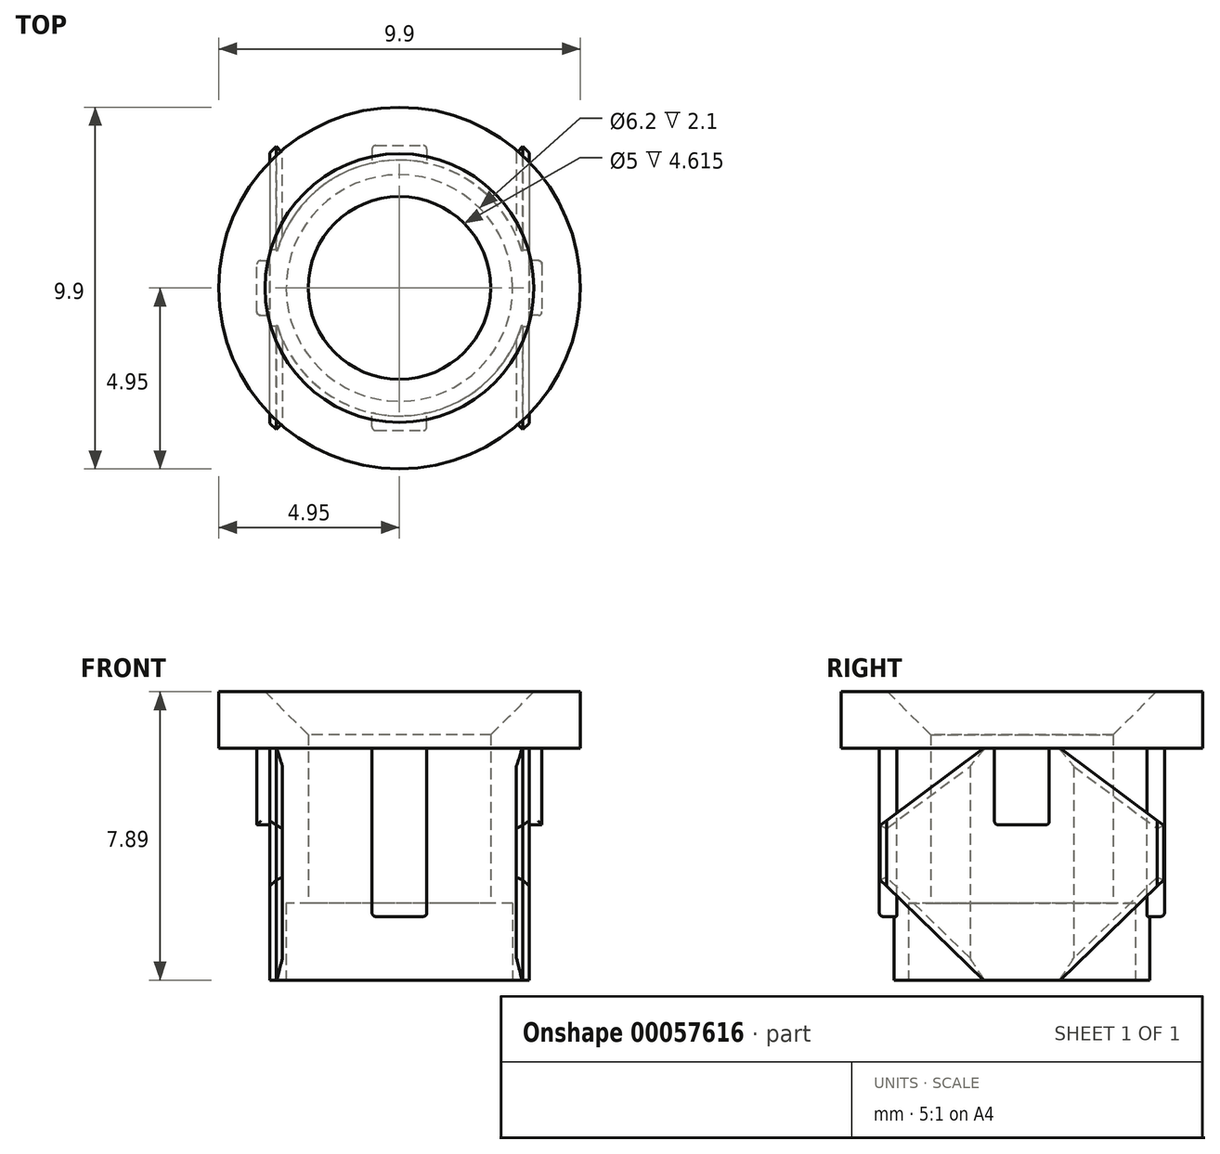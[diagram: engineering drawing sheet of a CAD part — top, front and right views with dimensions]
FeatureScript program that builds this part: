
annotation { "Feature Type Name" : "Feature", "Feature Type Description" : "" }
export const myFeature = defineFeature(function(context is Context, id is Id, definition is map)
    precondition{}
    {
        {
            var Q0;
            Q0=qCreatedBy(makeId("Top.planeOp"),FACE);
            var sketch = newSketch(context, id + "F0", { "sketchPlane" : qUnion([Q0])});
            skCircle(sketch, "E0", {"center": v(0, 0) * mm, "radius": 3.1 * mm});
            skCircle(sketch, "E1", {"center": v(0, 0) * mm, "radius": 3.5 * mm});
            skSolve(sketch);
        }
        {
            var Q0;
            Q0=makeQuery(id+"F0.imprint","IMPRINT",FACE,{"disambiguationData":[TD([[makeQuery(id+"F0.imprint","IMPRINT",EDGE,{"derivedFrom":sQuery(id+"F0.wireOp",EDGE,"E0")}),-1.0]])]});
            extrude(context, id + "F1", {"entities" : qUnion([Q0]), "depth" : 2.1 * mm});
        }
        {
            var Q0;
            Q0=makeQuery(id+"F1.opExtrude","CAP_FACE",FACE,{"disambiguationData":[OSD([sQuery(id+"F0.wireOp",EDGE,"E0"),sQuery(id+"F0.wireOp",EDGE,"E1")])],"isStart":false});
            var sketch = newSketch(context, id + "F2", { "sketchPlane" : qUnion([Q0])});
            skCircle(sketch, "E2", {"center": v(0, 0) * mm, "radius": 2.5 * mm});
            skSolve(sketch);
        }
        {
            var Q0;
            Q0=makeQuery(id+"F2.imprint","IMPRINT",FACE,{"disambiguationData":[TD([[makeQuery(id+"F2.imprint","IMPRINT",EDGE,{"derivedFrom":sQuery(id+"F2.wireOp",EDGE,"E2")}),-1.0]])]});
            var Q1;
            Q1=makeQuery(id+"F2.imprint","IMPRINT",FACE,{"disambiguationData":[TD([[makeQuery(id+"F2.imprint","IMPRINT",EDGE,{"derivedFrom":makeQuery(id+"F1.opExtrude","CAP_EDGE",EDGE,{"disambiguationData":[OSD([sQuery(id+"F0.wireOp",EDGE,"E0")])],"isStart":false})}),-1.0]])]});
            extrude(context, id + "F3", {"entities" : qUnion([Q0, Q1]), "operationType" : NewBodyOperationType.ADD, "depth" : 4.24 * mm});
        }
        {
            var Q0;
            Q0=makeQuery(id+"F3.opExtrude","CAP_FACE",FACE,{"disambiguationData":[OSD([sQuery(id+"F0.wireOp",EDGE,"E1"),sQuery(id+"F2.wireOp",EDGE,"E2")])],"isStart":false});
            var sketch = newSketch(context, id + "F4", { "sketchPlane" : qUnion([Q0])});
            skCircle(sketch, "E3", {"center": v(0, 0) * mm, "radius": 4.95 * mm});
            skCircle(sketch, "E4", {"center": v(0, 0) * mm, "radius": 2.5 * mm});
            skSolve(sketch);
        }
        {
            var Q0;
            Q0=makeQuery(id+"F4.imprint","IMPRINT",FACE,{"disambiguationData":[TD([[makeQuery(id+"F4.imprint","IMPRINT",EDGE,{"derivedFrom":sQuery(id+"F4.wireOp",EDGE,"E3")}),1.0]])]});
            var Q1;
            Q1=makeQuery(id+"F4.imprint","IMPRINT",FACE,{"disambiguationData":[TD([[makeQuery(id+"F4.imprint","IMPRINT",EDGE,{"derivedFrom":sQuery(id+"F4.wireOp",EDGE,"E4")}),-1.0]])]});
            extrude(context, id + "F5", {"entities" : qUnion([Q0, Q1]), "operationType" : NewBodyOperationType.ADD, "depth" : 1.55 * mm});
        }
        {
            var Q0;
            Q0=makeQuery(id+"F5.opExtrude","CAP_EDGE",EDGE,{"disambiguationData":[OSD([sQuery(id+"F4.wireOp",EDGE,"E4")])],"isStart":false});
            chamfer(context, id + "F6", {"entities" : qUnion([Q0]), "width" : 1.18 * mm, "tangentPropagation" : true});
        }
        {
            var Q0;
            Q0=makeQuery(id+"F5.opExtrude","CAP_FACE",FACE,{"disambiguationData":[OSD([sQuery(id+"F4.wireOp",EDGE,"E3"),sQuery(id+"F4.wireOp",EDGE,"E4")])],"isStart":true});
            var sketch = newSketch(context, id + "F7", { "sketchPlane" : qUnion([Q0])});
            skLineSegment(sketch, "E5", {"start": v(0, 3.5) * mm, "end": v(0, 3.68) * mm, "construction": true});
            skLineSegment(sketch, "E6", {"start": v(0, 3.5) * mm, "end": v(0, 3.7) * mm, "construction": true});
            skLineSegment(sketch, "E7", {"start": v(0, -3.5) * mm, "end": v(0, -3.9) * mm, "construction": true});
            skLineSegment(sketch, "E8", {"start": v(0, -3.9) * mm, "end": v(0.75, -3.9) * mm});
            skLineSegment(sketch, "E9", {"start": v(0, -3.9) * mm, "end": v(-0.75, -3.9) * mm});
            skLineSegment(sketch, "E10", {"start": v(0.75, -3.9) * mm, "end": v(0.75, -3.42) * mm});
            skLineSegment(sketch, "E11", {"start": v(-0.75, -3.9) * mm, "end": v(-0.75, -3.42) * mm});
            skLineSegment(sketch, "E12.MirrorCS", {"start": v(0, 3.5) * mm, "end": v(0, 3.9) * mm, "construction": true});
            skLineSegment(sketch, "E13.MirrorCS", {"start": v(0, 3.9) * mm, "end": v(-0.75, 3.9) * mm});
            skLineSegment(sketch, "E14.MirrorCS", {"start": v(0, 3.9) * mm, "end": v(0.75, 3.9) * mm});
            skLineSegment(sketch, "E15.MirrorCS", {"start": v(0.75, 3.9) * mm, "end": v(0.75, 3.42) * mm});
            skLineSegment(sketch, "E16.MirrorCS", {"start": v(-0.75, 3.9) * mm, "end": v(-0.75, 3.42) * mm});
            skLineSegment(sketch, "E17", {"start": v(0, 0) * mm, "end": v(-2.98, -2.98) * mm, "construction": true});
            skLineSegment(sketch, "E18.MirrorCS", {"start": v(0, 0) * mm, "end": v(2.98, -2.98) * mm, "construction": true});
            skLineSegment(sketch, "E19.MirrorCS", {"start": v(3.9, 0.75) * mm, "end": v(3.42, 0.75) * mm});
            skLineSegment(sketch, "E20.MirrorCS", {"start": v(3.9, 0) * mm, "end": v(3.9, 0.75) * mm});
            skLineSegment(sketch, "E21.MirrorCS", {"start": v(3.9, 0) * mm, "end": v(3.9, -0.75) * mm});
            skLineSegment(sketch, "E22.MirrorCS", {"start": v(3.9, -0.75) * mm, "end": v(3.42, -0.75) * mm});
            skLineSegment(sketch, "E23.MirrorCS", {"start": v(3.5, 0) * mm, "end": v(3.9, 0) * mm, "construction": true});
            skLineSegment(sketch, "E24.MirrorCS", {"start": v(-3.9, -0.75) * mm, "end": v(-3.42, -0.75) * mm});
            skLineSegment(sketch, "E25.MirrorCS", {"start": v(-3.5, 0) * mm, "end": v(-3.9, 0) * mm, "construction": true});
            skLineSegment(sketch, "E26.MirrorCS", {"start": v(-3.9, 0.75) * mm, "end": v(-3.42, 0.75) * mm});
            skLineSegment(sketch, "E27.MirrorCS", {"start": v(-3.9, 0) * mm, "end": v(-3.9, 0.75) * mm});
            skLineSegment(sketch, "E28.MirrorCS", {"start": v(-3.9, 0) * mm, "end": v(-3.9, -0.75) * mm});
            skSolve(sketch);
        }
        {
            var Q0;
            Q0=makeQuery(id+"F7.imprint","IMPRINT",FACE,{"disambiguationData":[TD([[makeQuery(id+"F7.imprint","IMPRINT",EDGE,{"derivedFrom":sQuery(id+"F7.wireOp",EDGE,"E8")}),1.0]])]});
            var Q1;
            Q1=makeQuery(id+"F7.imprint","IMPRINT",FACE,{"disambiguationData":[TD([[makeQuery(id+"F7.imprint","IMPRINT",EDGE,{"derivedFrom":sQuery(id+"F7.wireOp",EDGE,"E13.MirrorCS")}),1.0]])]});
            extrude(context, id + "F8", {"entities" : qUnion([Q0, Q1]), "operationType" : NewBodyOperationType.ADD, "depth" : 4.6 * mm});
        }
        {
            var Q0;
            {var subQ1=sQuery(id+"F7.wireOp",EDGE,"E24.MirrorCS");Q0=makeQuery(id+"F7.imprint","IMPRINT",FACE,{"disambiguationData":[TD([[makeQuery(id+"F7.imprint","IMPRINT",EDGE,{"derivedFrom":subQ1}),1.0]])]});}
            var Q1;
            {var subQ1=sQuery(id+"F7.wireOp",EDGE,"E19.MirrorCS");Q1=makeQuery(id+"F7.imprint","IMPRINT",FACE,{"disambiguationData":[TD([[makeQuery(id+"F7.imprint","IMPRINT",EDGE,{"derivedFrom":subQ1}),1.0]])]});}
            extrude(context, id + "F9", {"entities" : qUnion([Q0, Q1]), "operationType" : NewBodyOperationType.ADD, "depth" : 2.09 * mm});
        }
        {
            var Q0;
            Q0=makeQuery(id+"F8.opExtrude","CAP_EDGE",EDGE,{"disambiguationData":[OSD([sQuery(id+"F7.wireOp",EDGE,"E10")])],"isStart":false});
            var Q1;
            Q1=makeQuery(id+"F8.opExtrude","CAP_EDGE",EDGE,{"disambiguationData":[OSD([sQuery(id+"F7.wireOp",EDGE,"E8"),sQuery(id+"F7.wireOp",EDGE,"E9")])],"isStart":false});
            var Q2;
            Q2=makeQuery(id+"F8.opExtrude","SWEPT_EDGE",EDGE,{"disambiguationData":[OSD([sQuery(id+"F7.wireOp",EDGE,"E8"),sQuery(id+"F7.wireOp",EDGE,"E10")])]});
            var Q3;
            Q3=makeQuery(id+"F9.opExtrude","CAP_EDGE",EDGE,{"disambiguationData":[OSD([sQuery(id+"F7.wireOp",EDGE,"E22.MirrorCS")])],"isStart":false});
            var Q4;
            Q4=makeQuery(id+"F9.opExtrude","SWEPT_EDGE",EDGE,{"disambiguationData":[OSD([sQuery(id+"F7.wireOp",EDGE,"E21.MirrorCS"),sQuery(id+"F7.wireOp",EDGE,"E22.MirrorCS")])]});
            var Q5;
            Q5=makeQuery(id+"F9.opExtrude","CAP_EDGE",EDGE,{"disambiguationData":[OSD([sQuery(id+"F7.wireOp",EDGE,"E19.MirrorCS")])],"isStart":false});
            var Q6;
            Q6=makeQuery(id+"F9.opExtrude","SWEPT_EDGE",EDGE,{"disambiguationData":[OSD([sQuery(id+"F7.wireOp",EDGE,"E19.MirrorCS"),sQuery(id+"F7.wireOp",EDGE,"E20.MirrorCS")])]});
            var Q7;
            Q7=makeQuery(id+"F8.opExtrude","CAP_EDGE",EDGE,{"disambiguationData":[OSD([sQuery(id+"F7.wireOp",EDGE,"E13.MirrorCS"),sQuery(id+"F7.wireOp",EDGE,"E14.MirrorCS")])],"isStart":false});
            var Q8;
            Q8=makeQuery(id+"F8.opExtrude","SWEPT_EDGE",EDGE,{"disambiguationData":[OSD([sQuery(id+"F7.wireOp",EDGE,"E14.MirrorCS"),sQuery(id+"F7.wireOp",EDGE,"E15.MirrorCS")])]});
            var Q9;
            Q9=makeQuery(id+"F8.opExtrude","CAP_EDGE",EDGE,{"disambiguationData":[OSD([sQuery(id+"F7.wireOp",EDGE,"E15.MirrorCS")])],"isStart":false});
            var Q10;
            Q10=makeQuery(id+"F8.opExtrude","SWEPT_EDGE",EDGE,{"disambiguationData":[OSD([sQuery(id+"F7.wireOp",EDGE,"E13.MirrorCS"),sQuery(id+"F7.wireOp",EDGE,"E16.MirrorCS")])]});
            var Q11;
            Q11=makeQuery(id+"F8.opExtrude","CAP_EDGE",EDGE,{"disambiguationData":[OSD([sQuery(id+"F7.wireOp",EDGE,"E16.MirrorCS")])],"isStart":false});
            var Q12;
            Q12=makeQuery(id+"F9.opExtrude","SWEPT_EDGE",EDGE,{"disambiguationData":[OSD([sQuery(id+"F7.wireOp",EDGE,"E26.MirrorCS"),sQuery(id+"F7.wireOp",EDGE,"E27.MirrorCS")])]});
            var Q13;
            Q13=makeQuery(id+"F9.opExtrude","CAP_EDGE",EDGE,{"disambiguationData":[OSD([sQuery(id+"F7.wireOp",EDGE,"E27.MirrorCS"),sQuery(id+"F7.wireOp",EDGE,"E28.MirrorCS")])],"isStart":false});
            var Q14;
            Q14=makeQuery(id+"F9.opExtrude","SWEPT_EDGE",EDGE,{"disambiguationData":[OSD([sQuery(id+"F7.wireOp",EDGE,"E24.MirrorCS"),sQuery(id+"F7.wireOp",EDGE,"E28.MirrorCS")])]});
            var Q15;
            Q15=makeQuery(id+"F9.opExtrude","CAP_EDGE",EDGE,{"disambiguationData":[OSD([sQuery(id+"F7.wireOp",EDGE,"E24.MirrorCS")])],"isStart":false});
            var Q16;
            Q16=makeQuery(id+"F9.opExtrude","CAP_EDGE",EDGE,{"disambiguationData":[OSD([sQuery(id+"F7.wireOp",EDGE,"E26.MirrorCS")])],"isStart":false});
            var Q17;
            Q17=makeQuery(id+"F8.opExtrude","SWEPT_EDGE",EDGE,{"disambiguationData":[OSD([sQuery(id+"F7.wireOp",EDGE,"E9"),sQuery(id+"F7.wireOp",EDGE,"E11")])]});
            var Q18;
            Q18=makeQuery(id+"F8.opExtrude","CAP_EDGE",EDGE,{"disambiguationData":[OSD([sQuery(id+"F7.wireOp",EDGE,"E11")])],"isStart":false});
            fillet(context, id + "F10", {"entities" : qUnion([Q0, Q1, Q2, Q3, Q4, Q5, Q6, Q7, Q8, Q9, Q10, Q11, Q12, Q13, Q14, Q15, Q16, Q17, Q18]), "radius" : .1 * mm, "tangentPropagation" : true, "allowEdgeOverflow" : false});
        }
        {
            var Q0;
            Q0=makeQuery(id+"F7.imprint","IMPRINT",FACE,{"disambiguationData":[TD([[makeQuery(id+"F7.imprint","IMPRINT",EDGE,{"derivedFrom":sQuery(id+"F7.wireOp",EDGE,"E8")}),-1.0]])]});
            var sketch = newSketch(context, id + "F11", { "sketchPlane" : qUnion([Q0])});
            skLineSegment(sketch, "E29.bottom", {"start": v(3.2, 0) * mm, "end": v(3.55, 0) * mm});
            skLineSegment(sketch, "E29.top", {"start": v(3.2, -3.88) * mm, "end": v(3.55, -3.88) * mm});
            skLineSegment(sketch, "E29.left", {"start": v(3.2, 0) * mm, "end": v(3.2, -3.88) * mm});
            skLineSegment(sketch, "E29.right", {"start": v(3.55, 0) * mm, "end": v(3.55, -3.88) * mm});
            skLineSegment(sketch, "E30.top", {"start": v(3.2, 3.88) * mm, "end": v(3.55, 3.88) * mm});
            skLineSegment(sketch, "E30.left", {"start": v(3.2, 0) * mm, "end": v(3.2, 3.88) * mm});
            skLineSegment(sketch, "E30.right", {"start": v(3.55, 0) * mm, "end": v(3.55, 3.88) * mm});
            skSolve(sketch);
        }
        {
            var Q0;
            Q0 = qSketchRegion(id + "F11", true);
            extrude(context, id + "F12", {"entities" : qUnion([Q0]), "operationType" : NewBodyOperationType.ADD, "depth" : 6.34 * mm});
        }
        {
            var Q0;
            Q0=makeQuery(id+"F12.opExtrude","SWEPT_FACE",FACE,{"disambiguationData":[OSD([sQuery(id+"F11.wireOp",EDGE,"E29.right"),sQuery(id+"F11.wireOp",EDGE,"E30.right")])]});
            var sketch = newSketch(context, id + "F13", { "sketchPlane" : qUnion([Q0])});
            skLineSegment(sketch, "E31", {"start": v(-3.88, 4.24) * mm, "end": v(-1.05, 6.34) * mm});
            skLineSegment(sketch, "E32.MirrorCS", {"start": v(3.88, 4.24) * mm, "end": v(1.05, 6.34) * mm});
            skLineSegment(sketch, "E33", {"start": v(-3.88, 4.24) * mm, "end": v(-3.87, 2.74) * mm});
            skLineSegment(sketch, "E34", {"start": v(-3.87, 2.74) * mm, "end": v(-1.05, 0) * mm});
            skLineSegment(sketch, "E35.MirrorCS", {"start": v(3.88, 4.24) * mm, "end": v(3.87, 2.74) * mm});
            skLineSegment(sketch, "E36.MirrorCS", {"start": v(3.87, 2.74) * mm, "end": v(1.05, 0) * mm});
            skSolve(sketch);
        }
        {
            var Q0;
            {var subQ0=sQuery(id+"F13.wireOp",EDGE,"E31");Q0=makeQuery(id+"F13.imprint","IMPRINT",FACE,{"disambiguationData":[TD([[makeQuery(id+"F13.imprint","IMPRINT",EDGE,{"derivedFrom":subQ0}),1.0]])]});}
            var Q1;
            {var subQ0=sQuery(id+"F13.wireOp",EDGE,"E32.MirrorCS");Q1=makeQuery(id+"F13.imprint","IMPRINT",FACE,{"disambiguationData":[TD([[makeQuery(id+"F13.imprint","IMPRINT",EDGE,{"derivedFrom":subQ0}),-1.0]])]});}
            var Q2;
            {var subQ0=sQuery(id+"F13.wireOp",EDGE,"E36.MirrorCS");Q2=makeQuery(id+"F13.imprint","IMPRINT",FACE,{"disambiguationData":[TD([[makeQuery(id+"F13.imprint","IMPRINT",EDGE,{"derivedFrom":subQ0}),1.0]])]});}
            var Q3;
            {var subQ0=sQuery(id+"F13.wireOp",EDGE,"E34");Q3=makeQuery(id+"F13.imprint","IMPRINT",FACE,{"disambiguationData":[TD([[makeQuery(id+"F13.imprint","IMPRINT",EDGE,{"derivedFrom":subQ0}),-1.0]])]});}
            extrude(context, id + "F14", {"entities" : qUnion([Q0, Q1, Q2, Q3]), "operationType" : NewBodyOperationType.REMOVE, "oppositeDirection" : true, "depth" : 0.38 * mm});
        }
        {
            var Q0;
            Q0=makeQuery(id+"F1.opExtrude","SWEPT_BODY",BODY,{"disambiguationData":[OSD([sQuery(id+"F0.wireOp",EDGE,"E0"),sQuery(id+"F0.wireOp",EDGE,"E1")])]});
            var Q1;
            Q1=qCreatedBy(makeId("Right.planeOp"),FACE);
            mirror(context, id + "F15", {"operationType" : NewBodyOperationType.ADD, "entities" : qUnion([Q0]), "mirrorPlane" : qUnion([Q1])});
        }
        {
            var Q0;
            Q0=makeQuery(id+"F15.opPattern","COPY",EDGE,{"derivedFrom":makeQuery(id+"F14.boolean.opBoolean","COPY",EDGE,{"derivedFrom":makeQuery(id+"F14.opExtrude","CAP_EDGE",EDGE,{"disambiguationData":[OSD([sQuery(id+"F13.wireOp",EDGE,"E36.MirrorCS")])],"isStart":true})}),"instanceName":"1"});
            var Q1;
            Q1=makeQuery(id+"F15.opPattern","COPY",EDGE,{"derivedFrom":makeQuery(id+"F12.opExtrude","SWEPT_EDGE",EDGE,{"disambiguationData":[OSD([sQuery(id+"F11.wireOp",EDGE,"E29.top"),sQuery(id+"F11.wireOp",EDGE,"E29.right")])]}),"instanceName":"1"});
            var Q2;
            Q2=makeQuery(id+"F15.opPattern","COPY",EDGE,{"derivedFrom":makeQuery(id+"F14.boolean.opBoolean","COPY",EDGE,{"derivedFrom":makeQuery(id+"F14.opExtrude","CAP_EDGE",EDGE,{"disambiguationData":[OSD([sQuery(id+"F13.wireOp",EDGE,"E32.MirrorCS")])],"isStart":true})}),"instanceName":"1"});
            var Q3;
            {var subQ3=sQuery(id+"F11.wireOp",EDGE,"E30.left");var subQ6=sQuery(id+"F11.wireOp",EDGE,"E29.left");var subQ7=sQuery(id+"F11.wireOp",EDGE,"E29.top");Q3=makeQuery(id+"F15.opPattern","COPY",EDGE,{"derivedFrom":makeQuery(id+"F14.boolean.opBoolean","INTERSECT",EDGE,{"derivedFrom":[makeQuery(id+"F12.boolean.opBoolean","SPLIT",FACE,{"disambiguationData":[TD([makeQuery(id+"F12.opExtrude","SWEPT_FACE",FACE,{"disambiguationData":[OSD([subQ7])]})])],"derivedFrom":makeQuery(id+"F12.opExtrude","SWEPT_FACE",FACE,{"disambiguationData":[OSD([subQ6,subQ3])]})}),makeQuery(id+"F14.opExtrude","SWEPT_FACE",FACE,{"disambiguationData":[OSD([sQuery(id+"F13.wireOp",EDGE,"E36.MirrorCS")])]})]}),"instanceName":"1"});}
            var Q4;
            {var subQ3=sQuery(id+"F11.wireOp",EDGE,"E30.left");var subQ6=sQuery(id+"F11.wireOp",EDGE,"E29.left");var subQ7=sQuery(id+"F11.wireOp",EDGE,"E29.top");Q4=makeQuery(id+"F15.opPattern","COPY",EDGE,{"derivedFrom":makeQuery(id+"F14.boolean.opBoolean","INTERSECT",EDGE,{"derivedFrom":[makeQuery(id+"F12.boolean.opBoolean","SPLIT",FACE,{"disambiguationData":[TD([makeQuery(id+"F12.opExtrude","SWEPT_FACE",FACE,{"disambiguationData":[OSD([subQ7])]})])],"derivedFrom":makeQuery(id+"F12.opExtrude","SWEPT_FACE",FACE,{"disambiguationData":[OSD([subQ6,subQ3])]})}),makeQuery(id+"F14.opExtrude","SWEPT_FACE",FACE,{"disambiguationData":[OSD([sQuery(id+"F13.wireOp",EDGE,"E32.MirrorCS")])]})]}),"instanceName":"1"});}
            var Q5;
            Q5=makeQuery(id+"F15.opPattern","COPY",EDGE,{"derivedFrom":makeQuery(id+"F12.opExtrude","SWEPT_EDGE",EDGE,{"disambiguationData":[OSD([sQuery(id+"F11.wireOp",EDGE,"E29.top"),sQuery(id+"F11.wireOp",EDGE,"E29.left")])]}),"instanceName":"1"});
            var Q6;
            Q6=makeQuery(id+"F15.opPattern","COPY",EDGE,{"derivedFrom":makeQuery(id+"F14.boolean.opBoolean","COPY",EDGE,{"derivedFrom":makeQuery(id+"F14.opExtrude","CAP_EDGE",EDGE,{"disambiguationData":[OSD([sQuery(id+"F13.wireOp",EDGE,"E34")])],"isStart":true})}),"instanceName":"1"});
            var Q7;
            {var subQ3=sQuery(id+"F11.wireOp",EDGE,"E30.left");var subQ4=sQuery(id+"F11.wireOp",EDGE,"E30.top");var subQ6=sQuery(id+"F11.wireOp",EDGE,"E29.left");Q7=makeQuery(id+"F15.opPattern","COPY",EDGE,{"derivedFrom":makeQuery(id+"F14.boolean.opBoolean","INTERSECT",EDGE,{"derivedFrom":[makeQuery(id+"F12.boolean.opBoolean","SPLIT",FACE,{"disambiguationData":[TD([makeQuery(id+"F12.opExtrude","SWEPT_FACE",FACE,{"disambiguationData":[OSD([subQ4])]})])],"derivedFrom":makeQuery(id+"F12.opExtrude","SWEPT_FACE",FACE,{"disambiguationData":[OSD([subQ6,subQ3])]})}),makeQuery(id+"F14.opExtrude","SWEPT_FACE",FACE,{"disambiguationData":[OSD([sQuery(id+"F13.wireOp",EDGE,"E34")])]})]}),"instanceName":"1"});}
            var Q8;
            Q8=makeQuery(id+"F15.opPattern","COPY",EDGE,{"derivedFrom":makeQuery(id+"F12.opExtrude","SWEPT_EDGE",EDGE,{"disambiguationData":[OSD([sQuery(id+"F11.wireOp",EDGE,"E30.top"),sQuery(id+"F11.wireOp",EDGE,"E30.right")])]}),"instanceName":"1"});
            var Q9;
            Q9=makeQuery(id+"F15.opPattern","COPY",EDGE,{"derivedFrom":makeQuery(id+"F12.opExtrude","SWEPT_EDGE",EDGE,{"disambiguationData":[OSD([sQuery(id+"F11.wireOp",EDGE,"E30.top"),sQuery(id+"F11.wireOp",EDGE,"E30.left")])]}),"instanceName":"1"});
            var Q10;
            Q10=makeQuery(id+"F15.opPattern","COPY",EDGE,{"derivedFrom":makeQuery(id+"F14.boolean.opBoolean","COPY",EDGE,{"derivedFrom":makeQuery(id+"F14.opExtrude","CAP_EDGE",EDGE,{"disambiguationData":[OSD([sQuery(id+"F13.wireOp",EDGE,"E31")])],"isStart":true})}),"instanceName":"1"});
            var Q11;
            {var subQ3=sQuery(id+"F11.wireOp",EDGE,"E30.left");var subQ4=sQuery(id+"F11.wireOp",EDGE,"E30.top");var subQ6=sQuery(id+"F11.wireOp",EDGE,"E29.left");Q11=makeQuery(id+"F15.opPattern","COPY",EDGE,{"derivedFrom":makeQuery(id+"F14.boolean.opBoolean","INTERSECT",EDGE,{"derivedFrom":[makeQuery(id+"F12.boolean.opBoolean","SPLIT",FACE,{"disambiguationData":[TD([makeQuery(id+"F12.opExtrude","SWEPT_FACE",FACE,{"disambiguationData":[OSD([subQ4])]})])],"derivedFrom":makeQuery(id+"F12.opExtrude","SWEPT_FACE",FACE,{"disambiguationData":[OSD([subQ6,subQ3])]})}),makeQuery(id+"F14.opExtrude","SWEPT_FACE",FACE,{"disambiguationData":[OSD([sQuery(id+"F13.wireOp",EDGE,"E31")])]})]}),"instanceName":"1"});}
            var Q12;
            {var subQ3=sQuery(id+"F11.wireOp",EDGE,"E30.left");var subQ4=sQuery(id+"F11.wireOp",EDGE,"E30.top");var subQ6=sQuery(id+"F11.wireOp",EDGE,"E29.left");Q12=makeQuery(id+"F14.boolean.opBoolean","INTERSECT",EDGE,{"derivedFrom":[makeQuery(id+"F12.boolean.opBoolean","SPLIT",FACE,{"disambiguationData":[TD([makeQuery(id+"F12.opExtrude","SWEPT_FACE",FACE,{"disambiguationData":[OSD([subQ4])]})])],"derivedFrom":makeQuery(id+"F12.opExtrude","SWEPT_FACE",FACE,{"disambiguationData":[OSD([subQ6,subQ3])]})}),makeQuery(id+"F14.opExtrude","SWEPT_FACE",FACE,{"disambiguationData":[OSD([sQuery(id+"F13.wireOp",EDGE,"E31")])]})]});}
            var Q13;
            Q13=makeQuery(id+"F14.boolean.opBoolean","COPY",EDGE,{"derivedFrom":makeQuery(id+"F14.opExtrude","CAP_EDGE",EDGE,{"disambiguationData":[OSD([sQuery(id+"F13.wireOp",EDGE,"E31")])],"isStart":true})});
            var Q14;
            Q14=makeQuery(id+"F12.opExtrude","SWEPT_EDGE",EDGE,{"disambiguationData":[OSD([sQuery(id+"F11.wireOp",EDGE,"E30.top"),sQuery(id+"F11.wireOp",EDGE,"E30.left")])]});
            var Q15;
            Q15=makeQuery(id+"F12.opExtrude","SWEPT_EDGE",EDGE,{"disambiguationData":[OSD([sQuery(id+"F11.wireOp",EDGE,"E30.top"),sQuery(id+"F11.wireOp",EDGE,"E30.right")])]});
            var Q16;
            {var subQ3=sQuery(id+"F11.wireOp",EDGE,"E30.left");var subQ4=sQuery(id+"F11.wireOp",EDGE,"E30.top");var subQ6=sQuery(id+"F11.wireOp",EDGE,"E29.left");Q16=makeQuery(id+"F14.boolean.opBoolean","INTERSECT",EDGE,{"derivedFrom":[makeQuery(id+"F12.boolean.opBoolean","SPLIT",FACE,{"disambiguationData":[TD([makeQuery(id+"F12.opExtrude","SWEPT_FACE",FACE,{"disambiguationData":[OSD([subQ4])]})])],"derivedFrom":makeQuery(id+"F12.opExtrude","SWEPT_FACE",FACE,{"disambiguationData":[OSD([subQ6,subQ3])]})}),makeQuery(id+"F14.opExtrude","SWEPT_FACE",FACE,{"disambiguationData":[OSD([sQuery(id+"F13.wireOp",EDGE,"E34")])]})]});}
            var Q17;
            Q17=makeQuery(id+"F14.boolean.opBoolean","COPY",EDGE,{"derivedFrom":makeQuery(id+"F14.opExtrude","CAP_EDGE",EDGE,{"disambiguationData":[OSD([sQuery(id+"F13.wireOp",EDGE,"E34")])],"isStart":true})});
            var Q18;
            Q18=makeQuery(id+"F14.boolean.opBoolean","COPY",EDGE,{"derivedFrom":makeQuery(id+"F14.opExtrude","CAP_EDGE",EDGE,{"disambiguationData":[OSD([sQuery(id+"F13.wireOp",EDGE,"E36.MirrorCS")])],"isStart":true})});
            var Q19;
            Q19=makeQuery(id+"F12.opExtrude","SWEPT_EDGE",EDGE,{"disambiguationData":[OSD([sQuery(id+"F11.wireOp",EDGE,"E29.top"),sQuery(id+"F11.wireOp",EDGE,"E29.right")])]});
            var Q20;
            Q20=makeQuery(id+"F14.boolean.opBoolean","COPY",EDGE,{"derivedFrom":makeQuery(id+"F14.opExtrude","CAP_EDGE",EDGE,{"disambiguationData":[OSD([sQuery(id+"F13.wireOp",EDGE,"E32.MirrorCS")])],"isStart":true})});
            var Q21;
            {var subQ3=sQuery(id+"F11.wireOp",EDGE,"E30.left");var subQ6=sQuery(id+"F11.wireOp",EDGE,"E29.left");var subQ7=sQuery(id+"F11.wireOp",EDGE,"E29.top");Q21=makeQuery(id+"F14.boolean.opBoolean","INTERSECT",EDGE,{"derivedFrom":[makeQuery(id+"F12.boolean.opBoolean","SPLIT",FACE,{"disambiguationData":[TD([makeQuery(id+"F12.opExtrude","SWEPT_FACE",FACE,{"disambiguationData":[OSD([subQ7])]})])],"derivedFrom":makeQuery(id+"F12.opExtrude","SWEPT_FACE",FACE,{"disambiguationData":[OSD([subQ6,subQ3])]})}),makeQuery(id+"F14.opExtrude","SWEPT_FACE",FACE,{"disambiguationData":[OSD([sQuery(id+"F13.wireOp",EDGE,"E32.MirrorCS")])]})]});}
            var Q22;
            Q22=makeQuery(id+"F12.opExtrude","SWEPT_EDGE",EDGE,{"disambiguationData":[OSD([sQuery(id+"F11.wireOp",EDGE,"E29.top"),sQuery(id+"F11.wireOp",EDGE,"E29.left")])]});
            var Q23;
            {var subQ3=sQuery(id+"F11.wireOp",EDGE,"E30.left");var subQ6=sQuery(id+"F11.wireOp",EDGE,"E29.left");var subQ7=sQuery(id+"F11.wireOp",EDGE,"E29.top");Q23=makeQuery(id+"F14.boolean.opBoolean","INTERSECT",EDGE,{"derivedFrom":[makeQuery(id+"F12.boolean.opBoolean","SPLIT",FACE,{"disambiguationData":[TD([makeQuery(id+"F12.opExtrude","SWEPT_FACE",FACE,{"disambiguationData":[OSD([subQ7])]})])],"derivedFrom":makeQuery(id+"F12.opExtrude","SWEPT_FACE",FACE,{"disambiguationData":[OSD([subQ6,subQ3])]})}),makeQuery(id+"F14.opExtrude","SWEPT_FACE",FACE,{"disambiguationData":[OSD([sQuery(id+"F13.wireOp",EDGE,"E36.MirrorCS")])]})]});}
            chamfer(context, id + "F16", {"entities" : qUnion([Q0, Q1, Q2, Q3, Q4, Q5, Q6, Q7, Q8, Q9, Q10, Q11, Q12, Q13, Q14, Q15, Q16, Q17, Q18, Q19, Q20, Q21, Q22, Q23]), "width" : .175 * mm, "tangentPropagation" : true});
        }
    });
